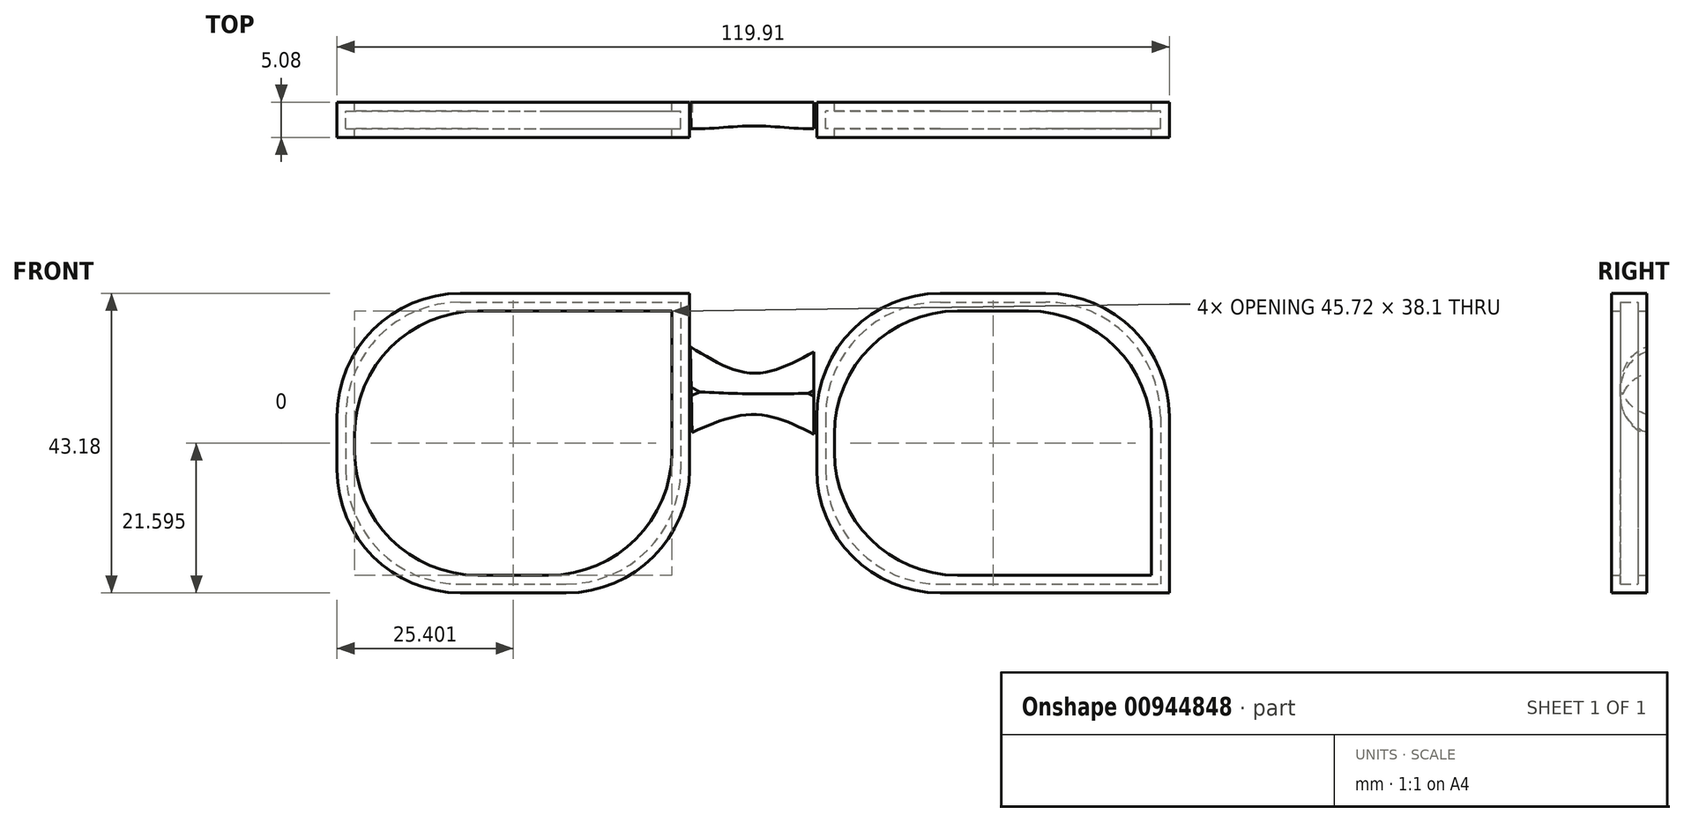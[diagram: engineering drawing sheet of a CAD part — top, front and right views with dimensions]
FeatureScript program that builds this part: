
annotation { "Feature Type Name" : "Feature", "Feature Type Description" : "" }
export const myFeature = defineFeature(function(context is Context, id is Id, definition is map)
    precondition{}
    {
        {
            var Q0;
            Q0=qCreatedBy(makeId("Front.planeOp"),FACE);
            var sketch = newSketch(context, id + "F0", { "sketchPlane" : qUnion([Q0])});
            skLineSegment(sketch, "E0.bottom", {"start": v(-66.35, 24.44) * mm, "end": v(-15.55, 24.44) * mm});
            skLineSegment(sketch, "E0.top", {"start": v(-66.35, -18.74) * mm, "end": v(-15.55, -18.74) * mm});
            skLineSegment(sketch, "E0.left", {"start": v(-66.35, 24.44) * mm, "end": v(-66.35, -18.74) * mm});
            skLineSegment(sketch, "E0.right", {"start": v(-15.55, 24.44) * mm, "end": v(-15.55, -18.74) * mm});
            skLineSegment(sketch, "E1.bottom", {"start": v(2.76, 24.44) * mm, "end": v(53.56, 24.44) * mm});
            skLineSegment(sketch, "E1.top", {"start": v(2.76, -18.74) * mm, "end": v(53.56, -18.74) * mm});
            skLineSegment(sketch, "E1.left", {"start": v(2.76, 24.44) * mm, "end": v(2.76, -18.74) * mm});
            skLineSegment(sketch, "E1.right", {"start": v(53.56, 24.44) * mm, "end": v(53.56, -18.74) * mm});
            skPoint(sketch, "E2.1.internal.snap0", {"position": v(-15.55, 2.85) * mm});
            skPoint(sketch, "E2.2.internal.snap0", {"position": v(2.76, 2.85) * mm});
            skLineSegment(sketch, "E3", {"start": v(-15.55, 19.11) * mm, "end": v(-15.55, 0) * mm});
            skLineSegment(sketch, "E4", {"start": v(2.76, 18.4) * mm, "end": v(2.76, 0) * mm});
            skSolve(sketch);
        }
        {
            var Q0;
            {var subQ1=sQuery(id+"F0.wireOp",EDGE,"E0.bottom");Q0=makeQuery(id+"F0.imprint","IMPRINT",FACE,{"disambiguationData":[TD([[makeQuery(id+"F0.imprint","IMPRINT",EDGE,{"derivedFrom":subQ1}),-1.0]])]});}
            var Q1;
            {var subQ3=sQuery(id+"F0.wireOp",EDGE,"E1.bottom");Q1=makeQuery(id+"F0.imprint","IMPRINT",FACE,{"disambiguationData":[TD([[makeQuery(id+"F0.imprint","IMPRINT",EDGE,{"derivedFrom":subQ3}),-1.0]])]});}
            extrude(context, id + "F1", {"entities" : qUnion([Q0, Q1]), "depth" : 5.08 * mm, "offsetDistance" : 25.4 * mm});
        }
        {
            var Q0;
            Q0=makeQuery(id+"F1.opExtrude","CAP_FACE",FACE,{"disambiguationData":[OSD([sQuery(id+"F0.wireOp",EDGE,"E0.bottom"),sQuery(id+"F0.wireOp",EDGE,"E0.top"),sQuery(id+"F0.wireOp",EDGE,"E0.left"),sQuery(id+"F0.wireOp",EDGE,"E0.right"),sQuery(id+"F0.wireOp",EDGE,"E3")])],"isStart":false});
            var Q1;
            Q1=makeQuery(id+"F1.opExtrude","CAP_FACE",FACE,{"disambiguationData":[OSD([sQuery(id+"F0.wireOp",EDGE,"E1.bottom"),sQuery(id+"F0.wireOp",EDGE,"E1.top"),sQuery(id+"F0.wireOp",EDGE,"E1.left"),sQuery(id+"F0.wireOp",EDGE,"E1.right"),sQuery(id+"F0.wireOp",EDGE,"E4")])],"isStart":false});
            var Q2;
            Q2=makeQuery(id+"F1.opExtrude","CAP_FACE",FACE,{"disambiguationData":[OSD([sQuery(id+"F0.wireOp",EDGE,"E1.bottom"),sQuery(id+"F0.wireOp",EDGE,"E1.top"),sQuery(id+"F0.wireOp",EDGE,"E1.left"),sQuery(id+"F0.wireOp",EDGE,"E1.right"),sQuery(id+"F0.wireOp",EDGE,"E4")])],"isStart":true});
            var Q3;
            Q3=makeQuery(id+"F1.opExtrude","CAP_FACE",FACE,{"disambiguationData":[OSD([sQuery(id+"F0.wireOp",EDGE,"E0.bottom"),sQuery(id+"F0.wireOp",EDGE,"E0.top"),sQuery(id+"F0.wireOp",EDGE,"E0.left"),sQuery(id+"F0.wireOp",EDGE,"E0.right"),sQuery(id+"F0.wireOp",EDGE,"E3")])],"isStart":true});
            shell(context, id + "F2", {"entities" : qUnion([Q0, Q1, Q2, Q3]), "thickness" : 2.54 * mm});
        }
        {
            var Q0;
            Q0=makeQuery(id+"F1.opExtrude","SWEPT_EDGE",EDGE,{"disambiguationData":[OSD([sQuery(id+"F0.wireOp",EDGE,"E0.top"),sQuery(id+"F0.wireOp",EDGE,"E0.left")])]});
            var Q1;
            Q1=makeQuery(id+"F1.opExtrude","SWEPT_EDGE",EDGE,{"disambiguationData":[OSD([sQuery(id+"F0.wireOp",EDGE,"E0.top"),sQuery(id+"F0.wireOp",EDGE,"E0.right")])]});
            var Q2;
            Q2=makeQuery(id+"F2.opShell","OFFSET_EDGE",EDGE,{"disambiguationData":[OSD([sQuery(id+"F0.wireOp",EDGE,"E0.top"),sQuery(id+"F0.wireOp",EDGE,"E0.right")])]});
            var Q3;
            Q3=makeQuery(id+"F2.opShell","OFFSET_EDGE",EDGE,{"disambiguationData":[OSD([sQuery(id+"F0.wireOp",EDGE,"E0.top"),sQuery(id+"F0.wireOp",EDGE,"E0.left")])]});
            var Q4;
            Q4=makeQuery(id+"F1.opExtrude","SWEPT_EDGE",EDGE,{"disambiguationData":[OSD([sQuery(id+"F0.wireOp",EDGE,"E1.bottom"),sQuery(id+"F0.wireOp",EDGE,"E1.left")])]});
            var Q5;
            Q5=makeQuery(id+"F1.opExtrude","SWEPT_EDGE",EDGE,{"disambiguationData":[OSD([sQuery(id+"F0.wireOp",EDGE,"E1.bottom"),sQuery(id+"F0.wireOp",EDGE,"E1.right")])]});
            var Q6;
            Q6=makeQuery(id+"F2.opShell","OFFSET_EDGE",EDGE,{"disambiguationData":[OSD([sQuery(id+"F0.wireOp",EDGE,"E1.bottom"),sQuery(id+"F0.wireOp",EDGE,"E1.right")])]});
            var Q7;
            Q7=makeQuery(id+"F2.opShell","OFFSET_EDGE",EDGE,{"disambiguationData":[OSD([sQuery(id+"F0.wireOp",EDGE,"E1.bottom"),sQuery(id+"F0.wireOp",EDGE,"E1.left")])]});
            var Q8;
            Q8=makeQuery(id+"F1.opExtrude","SWEPT_EDGE",EDGE,{"disambiguationData":[OSD([sQuery(id+"F0.wireOp",EDGE,"E0.bottom"),sQuery(id+"F0.wireOp",EDGE,"E0.left")])]});
            var Q9;
            Q9=makeQuery(id+"F2.opShell","OFFSET_EDGE",EDGE,{"disambiguationData":[OSD([sQuery(id+"F0.wireOp",EDGE,"E0.bottom"),sQuery(id+"F0.wireOp",EDGE,"E0.left")])]});
            var Q10;
            Q10=makeQuery(id+"F1.opExtrude","SWEPT_EDGE",EDGE,{"disambiguationData":[OSD([sQuery(id+"F0.wireOp",EDGE,"E1.top"),sQuery(id+"F0.wireOp",EDGE,"E1.left")])]});
            var Q11;
            Q11=makeQuery(id+"F2.opShell","OFFSET_EDGE",EDGE,{"disambiguationData":[OSD([sQuery(id+"F0.wireOp",EDGE,"E1.top"),sQuery(id+"F0.wireOp",EDGE,"E1.left")])]});
            fillet(context, id + "F3", {"entities" : qUnion([Q0, Q1, Q2, Q3, Q4, Q5, Q6, Q7, Q8, Q9, Q10, Q11]), "radius" : 17.78 * mm, "tangentPropagation" : true, "allowEdgeOverflow" : false});
        }
        {
            var Q0;
            Q0=qCreatedBy(makeId("Front.planeOp"),FACE);
            var sketch = newSketch(context, id + "F4", { "sketchPlane" : qUnion([Q0])});
            skFitSpline(sketch, "E5", {"points": [v(-15.43, 16.74) * mm, v(-6.41, 12.94) * mm, v(2.37, 16.03) * mm], "startDerivative": vector(17.83, -10.99) * mm, "endDerivative": vector(17.78, 9.65) * mm});
            skFitSpline(sketch, "E6", {"points": [v(-15.2, 4.4) * mm, v(-6.17, 7) * mm, v(2.37, 4.15) * mm], "startDerivative": vector(18, 7.93) * mm, "endDerivative": vector(17.13, -8.46) * mm});
            skLineSegment(sketch, "E7", {"start": v(-15.43, 16.74) * mm, "end": v(-15.2, 4.4) * mm});
            skLineSegment(sketch, "E8", {"start": v(2.37, 16.03) * mm, "end": v(2.37, 4.15) * mm});
            skSolve(sketch);
        }
        {
            var Q0;
            Q0=makeQuery(id+"F4.imprint","IMPRINT",FACE,{"disambiguationData":[TD([[makeQuery(id+"F4.imprint","IMPRINT",EDGE,{"derivedFrom":sQuery(id+"F4.wireOp",EDGE,"E5")}),-1.0]])]});
            extrude(context, id + "F5", {"entities" : qUnion([Q0]), "depth" : 3.8 * mm, "offsetDistance" : 25.4 * mm});
        }
        {
            var Q0;
            Q0=makeQuery(id+"F2.opShell","OFFSET_FACE",FACE,{"disambiguationData":[OSD([sQuery(id+"F0.wireOp",EDGE,"E0.right"),sQuery(id+"F0.wireOp",EDGE,"E3")])]});
            var Q1;
            {var subQ0=sQuery(id+"F0.wireOp",EDGE,"E0.right");var subQ1=sQuery(id+"F0.wireOp",EDGE,"E0.bottom");Q1=makeQuery(id+"F3.opFillet","BLEND_FACE",FACE,{"disambiguationData":[OSD([subQ1,subQ0]),TDD([makeQuery(id+"F2.opShell","OFFSET_EDGE",EDGE,{"disambiguationData":[OSD([subQ1,subQ0])]})])]});}
            var Q2;
            Q2=makeQuery(id+"F2.opShell","OFFSET_FACE",FACE,{"disambiguationData":[OSD([sQuery(id+"F0.wireOp",EDGE,"E0.bottom")])]});
            var Q3;
            {var subQ0=sQuery(id+"F0.wireOp",EDGE,"E0.right");var subQ1=sQuery(id+"F0.wireOp",EDGE,"E0.top");Q3=makeQuery(id+"F3.opFillet","BLEND_FACE",FACE,{"disambiguationData":[OSD([subQ1,subQ0]),TDD([makeQuery(id+"F2.opShell","OFFSET_EDGE",EDGE,{"disambiguationData":[OSD([subQ1,subQ0])]})])]});}
            var Q4;
            Q4=makeQuery(id+"F2.opShell","OFFSET_FACE",FACE,{"disambiguationData":[OSD([sQuery(id+"F0.wireOp",EDGE,"E0.top")])]});
            var Q5;
            {var subQ0=sQuery(id+"F0.wireOp",EDGE,"E0.left");var subQ1=sQuery(id+"F0.wireOp",EDGE,"E0.top");Q5=makeQuery(id+"F3.opFillet","BLEND_FACE",FACE,{"disambiguationData":[OSD([subQ1,subQ0]),TDD([makeQuery(id+"F2.opShell","OFFSET_EDGE",EDGE,{"disambiguationData":[OSD([subQ1,subQ0])]})])]});}
            var Q6;
            Q6=makeQuery(id+"F2.opShell","OFFSET_FACE",FACE,{"disambiguationData":[OSD([sQuery(id+"F0.wireOp",EDGE,"E0.left")])]});
            var Q7;
            {var subQ0=sQuery(id+"F0.wireOp",EDGE,"E0.left");var subQ1=sQuery(id+"F0.wireOp",EDGE,"E0.bottom");Q7=makeQuery(id+"F3.opFillet","BLEND_FACE",FACE,{"disambiguationData":[OSD([subQ1,subQ0]),TDD([makeQuery(id+"F2.opShell","OFFSET_EDGE",EDGE,{"disambiguationData":[OSD([subQ1,subQ0])]})])]});}
            shell(context, id + "F6", {"entities" : qUnion([Q0, Q1, Q2, Q3, Q4, Q5, Q6, Q7]), "thickness" : 1.27 * mm});
        }
        {
            var Q0;
            Q0=makeQuery(id+"F2.opShell","OFFSET_FACE",FACE,{"disambiguationData":[OSD([sQuery(id+"F0.wireOp",EDGE,"E1.right")])]});
            var Q1;
            {var subQ0=sQuery(id+"F0.wireOp",EDGE,"E1.right");var subQ1=sQuery(id+"F0.wireOp",EDGE,"E1.bottom");Q1=makeQuery(id+"F3.opFillet","BLEND_FACE",FACE,{"disambiguationData":[OSD([subQ1,subQ0]),TDD([makeQuery(id+"F2.opShell","OFFSET_EDGE",EDGE,{"disambiguationData":[OSD([subQ1,subQ0])]})])]});}
            var Q2;
            {var subQ0=sQuery(id+"F0.wireOp",EDGE,"E1.right");var subQ1=sQuery(id+"F0.wireOp",EDGE,"E1.top");Q2=makeQuery(id+"F3.opFillet","BLEND_FACE",FACE,{"disambiguationData":[OSD([subQ1,subQ0]),TDD([makeQuery(id+"F2.opShell","OFFSET_EDGE",EDGE,{"disambiguationData":[OSD([subQ1,subQ0])]})])]});}
            var Q3;
            Q3=makeQuery(id+"F2.opShell","OFFSET_FACE",FACE,{"disambiguationData":[OSD([sQuery(id+"F0.wireOp",EDGE,"E1.top")])]});
            var Q4;
            {var subQ0=sQuery(id+"F0.wireOp",EDGE,"E1.left");var subQ1=sQuery(id+"F0.wireOp",EDGE,"E1.top");Q4=makeQuery(id+"F3.opFillet","BLEND_FACE",FACE,{"disambiguationData":[OSD([subQ1,subQ0]),TDD([makeQuery(id+"F2.opShell","OFFSET_EDGE",EDGE,{"disambiguationData":[OSD([subQ1,subQ0])]})])]});}
            var Q5;
            Q5=makeQuery(id+"F2.opShell","OFFSET_FACE",FACE,{"disambiguationData":[OSD([sQuery(id+"F0.wireOp",EDGE,"E1.left"),sQuery(id+"F0.wireOp",EDGE,"E4")])]});
            var Q6;
            {var subQ0=sQuery(id+"F0.wireOp",EDGE,"E1.left");var subQ1=sQuery(id+"F0.wireOp",EDGE,"E1.bottom");Q6=makeQuery(id+"F3.opFillet","BLEND_FACE",FACE,{"disambiguationData":[OSD([subQ1,subQ0]),TDD([makeQuery(id+"F2.opShell","OFFSET_EDGE",EDGE,{"disambiguationData":[OSD([subQ1,subQ0])]})])]});}
            var Q7;
            Q7=makeQuery(id+"F2.opShell","OFFSET_FACE",FACE,{"disambiguationData":[OSD([sQuery(id+"F0.wireOp",EDGE,"E1.bottom")])]});
            shell(context, id + "F7", {"entities" : qUnion([Q0, Q1, Q2, Q3, Q4, Q5, Q6, Q7]), "thickness" : 1.27 * mm});
        }
        {
            var Q0;
            Q0=makeQuery(id+"F5.opExtrude","CAP_EDGE",EDGE,{"disambiguationData":[OSD([sQuery(id+"F4.wireOp",EDGE,"E5")])],"isStart":false});
            var Q1;
            Q1=makeQuery(id+"F5.opExtrude","CAP_EDGE",EDGE,{"disambiguationData":[OSD([sQuery(id+"F4.wireOp",EDGE,"E6")])],"isStart":false});
            fillet(context, id + "F8", {"entities" : qUnion([Q0, Q1]), "radius" : 5.08 * mm, "tangentPropagation" : true, "allowEdgeOverflow" : false});
        }
    });
